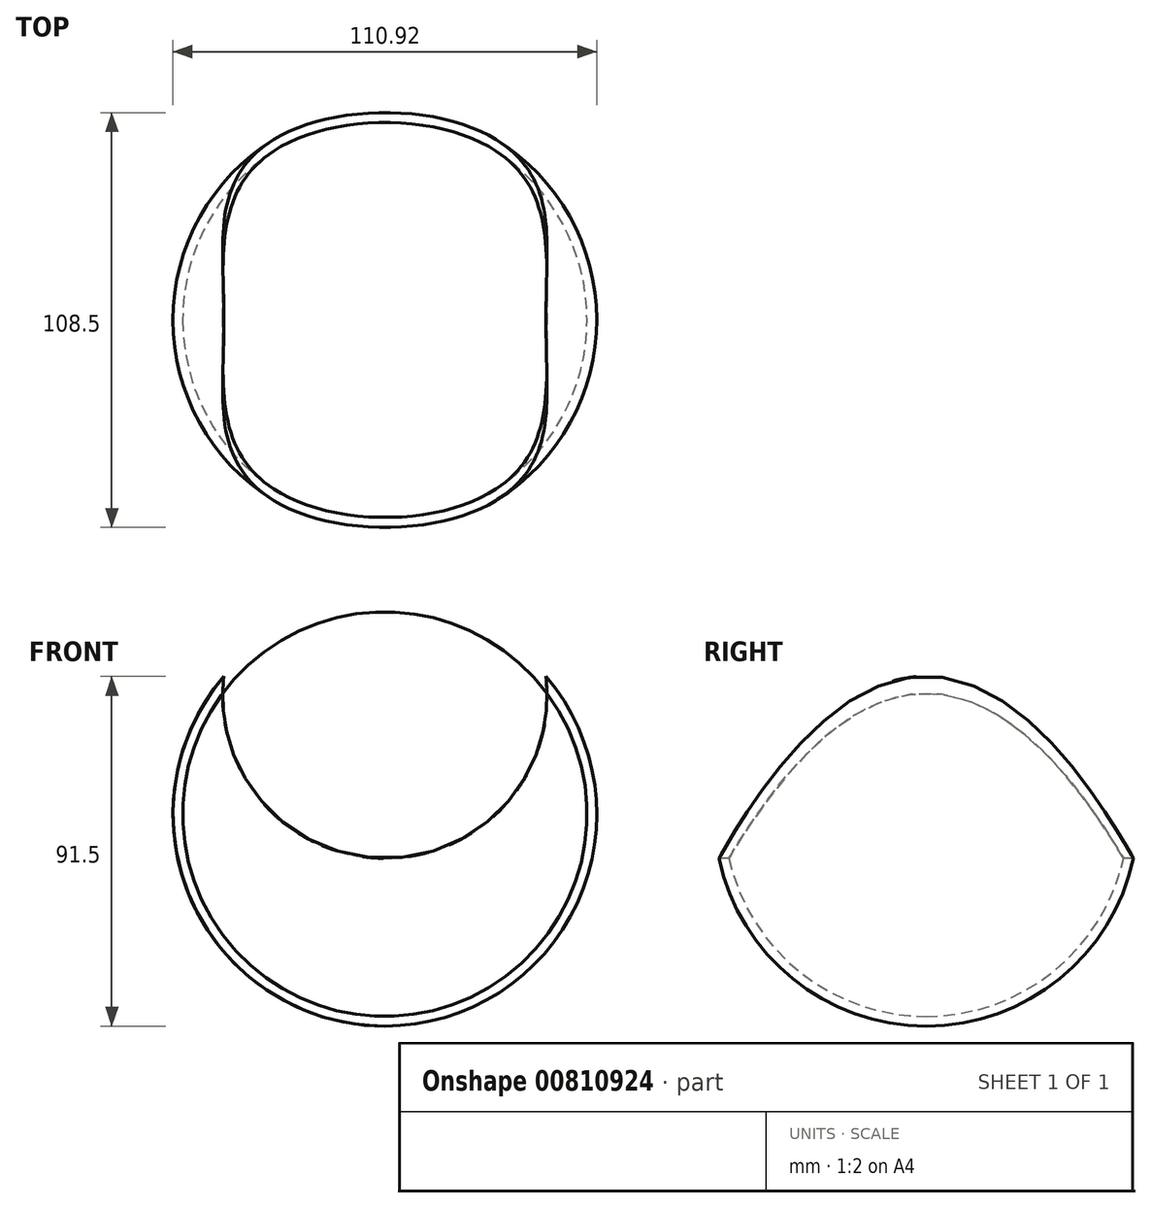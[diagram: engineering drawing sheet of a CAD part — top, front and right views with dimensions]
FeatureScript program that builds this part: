
annotation { "Feature Type Name" : "Feature", "Feature Type Description" : "" }
export const myFeature = defineFeature(function(context is Context, id is Id, definition is map)
    precondition{}
    {
        {
            var Q0;
            Q0=qCreatedBy(makeId("Front.planeOp"),FACE);
            var sketch = newSketch(context, id + "F0", { "sketchPlane" : qUnion([Q0])});
            skArc(sketch, "E0", {"start": v(0, -55.46) * mm, "mid": v(14, -53.67) * mm, "end": v(27.08, -48.4) * mm});
            skLineSegment(sketch, "E1", {"start": v(0, 55.46) * mm, "end": v(0, -55.46) * mm});
            skArc(sketch, "E2", {"start": v(27.08, -48.4) * mm, "mid": v(53.67, 14) * mm, "end": v(0, 55.46) * mm});
            skArc(sketch, "E3.trimOffspring", {"start": v(27.77, 48) * mm, "mid": v(14.38, 53.57) * mm, "end": v(0, 55.46) * mm});
            skSolve(sketch);
        }
        {
            var Q0;
            Q0=makeQuery(id+"F0.imprint","IMPRINT",FACE,{"disambiguationData":[TD([[makeQuery(id+"F0.imprint","IMPRINT",EDGE,{"derivedFrom":sQuery(id+"F0.wireOp",EDGE,"E0")}),1.0]])]});
            var Q1;
            Q1=sQuery(id+"F0.wireOp",EDGE,"E1");
            revolve(context, id + "F1", {"surfaceOperationType" : NewSurfaceOperationType.NEW, "entities" : qUnion([Q0]), "axis" : qUnion([Q1]), "revolveType" : RevolveType.FULL});
        }
        {
            var Q0;
            Q0=qCreatedBy(makeId("Front.planeOp"),FACE);
            var sketch = newSketch(context, id + "F2", { "sketchPlane" : qUnion([Q0])});
            skArc(sketch, "E4", {"start": v(-8.94, 64) * mm, "mid": v(-34.4, 25.94) * mm, "end": v(3.33, 0) * mm});
            skArc(sketch, "E5.MirrorCS", {"start": v(8.94, 64) * mm, "mid": v(34.4, 25.94) * mm, "end": v(-3.33, 0) * mm});
            skArc(sketch, "E6.0", {"start": v(-7.98, 63.45) * mm, "mid": v(-34.11, 29.03) * mm, "end": v(-1.9, 0.23) * mm});
            skArc(sketch, "E7.0", {"start": v(-7.62, 52.59) * mm, "mid": v(-23.35, 29.13) * mm, "end": v(-1.74, 10.93) * mm});
            skArc(sketch, "E8.0", {"start": v(7.96, 53.55) * mm, "mid": v(24.37, 29.1) * mm, "end": v(2.03, 9.9) * mm});
            skLineSegment(sketch, "E9", {"start": v(-7.62, 52.59) * mm, "end": v(7.96, 53.55) * mm});
            skLineSegment(sketch, "E10", {"start": v(8.94, 64) * mm, "end": v(-7.98, 63.45) * mm});
            skLineSegment(sketch, "E11", {"start": v(2.03, 9.9) * mm, "end": v(-1.74, 10.93) * mm});
            skLineSegment(sketch, "E12", {"start": v(3.33, 0) * mm, "end": v(-3.33, 0) * mm});
            skSolve(sketch);
        }
        {
            var Q0;
            Q0 = qSketchRegion(id + "F2", true);
            extrude(context, id + "F3", {"entities" : qUnion([Q0]), "operationType" : NewBodyOperationType.REMOVE, "endBound" : BoundingType.SYMMETRIC, "oppositeDirection" : true, "depth" : 148.84 * mm, "offsetDistance" : 25.4 * mm});
        }
        {
            var Q0;
            Q0=makeQuery(id+"F3.boolean.opBoolean","COPY",FACE,{"derivedFrom":makeQuery(id+"F3.opExtrude","SWEPT_FACE",FACE,{"disambiguationData":[OSD([sQuery(id+"F2.wireOp",EDGE,"E7.0")])]})});
            var Q1;
            Q1=makeQuery(id+"F3.boolean.opBoolean","COPY",FACE,{"derivedFrom":makeQuery(id+"F3.opExtrude","SWEPT_FACE",FACE,{"disambiguationData":[OSD([sQuery(id+"F2.wireOp",EDGE,"E8.0")])]})});
            var Q2;
            Q2=makeQuery(id+"F3.boolean.opBoolean","COPY",FACE,{"derivedFrom":makeQuery(id+"F3.opExtrude","SWEPT_FACE",FACE,{"disambiguationData":[OSD([sQuery(id+"F2.wireOp",EDGE,"E9")])]})});
            var Q3;
            Q3=makeQuery(id+"F3.boolean.opBoolean","COPY",FACE,{"derivedFrom":makeQuery(id+"F3.opExtrude","SWEPT_FACE",FACE,{"disambiguationData":[OSD([sQuery(id+"F2.wireOp",EDGE,"E11")])]})});
            shell(context, id + "F4", {"entities" : qUnion([Q0, Q1, Q2, Q3]), "thickness" : 2.54 * mm});
        }
        {
            var Q0;
            Q0=qCreatedBy(makeId("Front.planeOp"),FACE);
            var sketch = newSketch(context, id + "F5", { "sketchPlane" : qUnion([Q0])});
            skCircle(sketch, "E13", {"center": v(0, 30.93) * mm, "radius": 42.47 * mm});
            skSolve(sketch);
        }
        {
            var Q0;
            Q0 = qSketchRegion(id + "F5", true);
            extrude(context, id + "F6", {"entities" : qUnion([Q0]), "operationType" : NewBodyOperationType.REMOVE, "endBound" : BoundingType.SYMMETRIC, "oppositeDirection" : true, "depth" : 179.83 * mm, "offsetDistance" : 25.4 * mm});
        }
    });
